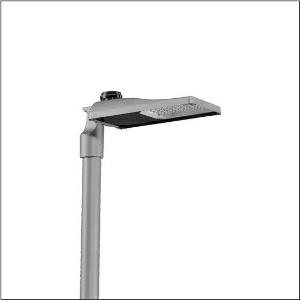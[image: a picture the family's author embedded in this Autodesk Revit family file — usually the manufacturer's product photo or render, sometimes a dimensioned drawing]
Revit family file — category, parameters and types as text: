
# Revit family: streetlight_sl_31_mini___st1_0a_5xh6d3bn08ha_24b0
name_source: partatom
category: Lighting Fixtures
units: mm (PartAtom-declared; Revit-internal decimal feet)

## family parameters
Cut with Voids When Loaded = No
Host = Face
Light Source = No
Part Type = Normal
Room Calculation Point = No
Round Connector Dimension = Use Diameter
Shared = No

## types (1)
- --- (1 x LED, 9240 lm, 68.3 W, 3000K)
    Apparent Load = 68 VA
    CIE Flux Codes = 37 72 97 100 100
    Color Rendering = 70
    Color Temperature = 3000K
    Default Elevation = 1800 mm
    Description = Streetlight SL 31 mini NEMA (7pin) mast luminaire for post-top, side-entry; light control with lens of PMMA; light distribution: ST1.0a, direct asymmetric distribution, for standard-compliant lighting for roads and squares; LED: luminous flux: 9.240lm, light colour: 730, colour temperature: 3000K; luminous efficacy: 135,3lm/W; control: pre-setting: linear dimming characteristic, flexible luminous flux parameterisation, time-dependent luminous flux control, constant luminous flux control, intelligent temperature release in ECG and LED module, overheat protection; luminaire housing, of diecast aluminium, Siteco® metallic grey (DB 702S), corrosivity category C5 high according to DIN EN ISO 12944; cover of toughened safety glass, transparent, opened without tools; mast flange of diecast aluminium, Siteco® metallic grey (DB 702S), spigot size: 76/60mm, mast flange included unmounted; with cable H07RN-F 3x 1.5mm², cable length: 8,5m, connection cable pre-assembled; mains connection: 220..240V, AC, 50/60Hz; power consumption (at start of service life): 68,3W / (at end of service life): 74,8W / (with reduced operation 50%): 29,7W; protection rating (complete): IP66; insulation class (complete): insulation class I (protective earthing); impact resistance: IK09; certification: CE, ENEC, ENEC+, VDE, UKCA; permissible operating ambient temperature for outdoor applications: -40..+50°C; packaging unit: 1 piece

Light Distribution: ST1.0a
    Height = 76 mm
    Lamp = 1 x LED
    Lamp Light Flux = 9240 lm
    Lamp Power = 68.3 W
    Lamp count = 1
    Length = 547 mm
    Luminous efficacy = 135 lm/W
    Manufacturer = Siteco
    ModVariant = No
    Model = 5XH6D3BN08HA
    Number of Poles = 1
    OnlyDefault = Yes
    Power Factor = 1
    Product Name = Streetlight SL 31 mini | ST1.0a
    Product group = mast luminaire | pylon top
    ProductGroupID = 6100
    Protection Class = Protection class I
    Protection Degree = IP 66
    RLX_Detail_Level = 1
    RLX_Emergency_Light_Flux = 0 lm
    RLX_Emergency_Type = 0
    RLX_Emergency_Type_DB = No
    RlxData = <blob elided: 40061 chars, md5=648a99c8>
    Socket = socket
    Standby Power = 0 W
    System Light Flux = 9240 lm
    System Power = 68 W
    Type Comments = factory setting: luminous flux: 100 % | dim-lin: 254 | 693 mA
    Type Image = l_1300322.jpg
    URL = http://relux.com
    VarID = @adj_050648
    Voltage = 0 V
    Weight = 0.00 kg
    Width = 265 mm

## geometry (parser evidence)
native form markers: Blend x4, Sweep x11
no freeform markers — native parametric forms only
